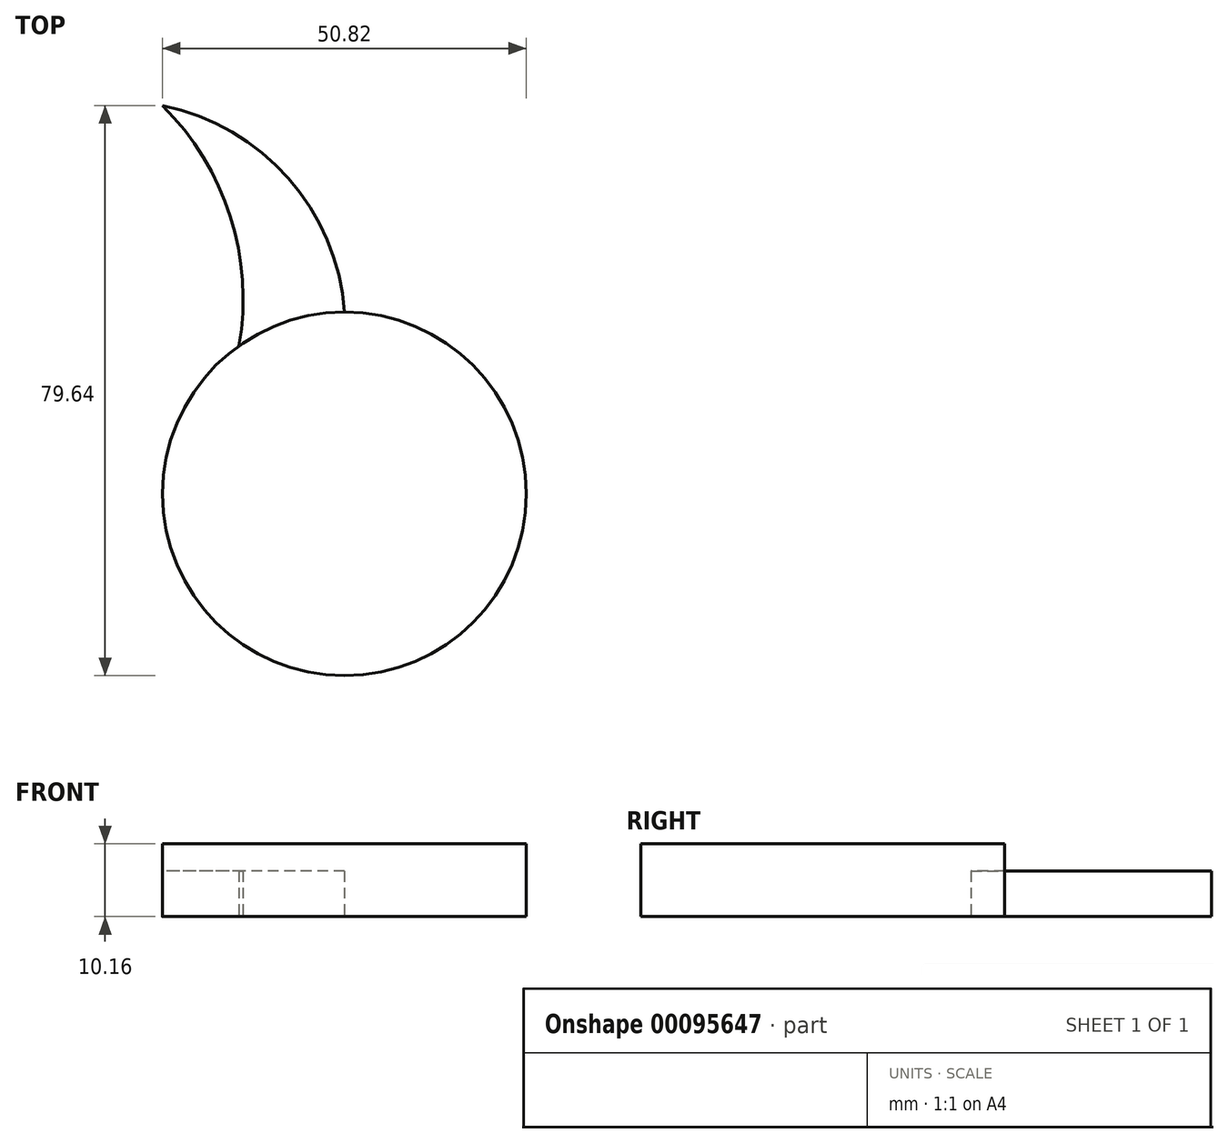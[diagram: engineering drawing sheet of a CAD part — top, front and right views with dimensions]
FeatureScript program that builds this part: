
annotation { "Feature Type Name" : "Feature", "Feature Type Description" : "" }
export const myFeature = defineFeature(function(context is Context, id is Id, definition is map)
    precondition{}
    {
        {
            var Q0;
            Q0=qCreatedBy(makeId("Top.planeOp"),FACE);
            var sketch = newSketch(context, id + "F0", { "sketchPlane" : qUnion([Q0])});
            skCircle(sketch, "E0", {"center": v(0, 0) * mm, "radius": 25.4 * mm});
            skArc(sketch, "E1", {"start": v(0, 25.4) * mm, "mid": v(-7.85, 44.1) * mm, "end": v(-25.42, 54.24) * mm});
            skPoint(sketch, "E1.first.point", {"position": v(0, 25.4) * mm});
            skPoint(sketch, "E1.second.point", {"position": v(-25.42, 54.24) * mm});
            skPoint(sketch, "E2.second.point", {"position": v(-14.73, 20.7) * mm});
            skArc(sketch, "E3.trimOffspring", {"start": v(-14.73, 20.7) * mm, "mid": v(-15.95, 38.78) * mm, "end": v(-25.42, 54.24) * mm});
            skSolve(sketch);
        }
        {
            var Q0;
            {var subQ0=sQuery(id+"F0.wireOp",EDGE,"E0");var subQ1=makeQuery(id+"F0.imprint","INTERSECT",VERTEX,{"derivedFrom":[subQ0,sQuery(id+"F0.wireOp",EDGE,"E1")]});Q0=makeQuery(id+"F0.imprint","IMPRINT",FACE,{"disambiguationData":[TD([[makeQuery(id+"F0.imprint","IMPRINT",EDGE,{"disambiguationData":[TD([[subQ1,-1.0]])],"derivedFrom":subQ0}),1.0]])]});}
            extrude(context, id + "F1", {"entities" : qUnion([Q0]), "depth" : 10.16 * mm});
        }
        {
            var Q0;
            {var subQ0=sQuery(id+"F0.wireOp",EDGE,"E1");Q0=makeQuery(id+"F0.imprint","IMPRINT",FACE,{"disambiguationData":[TD([[makeQuery(id+"F0.imprint","IMPRINT",EDGE,{"derivedFrom":subQ0}),1.0]])]});}
            extrude(context, id + "F2", {"entities" : qUnion([Q0]), "depth" : 6.35 * mm});
        }
    });
